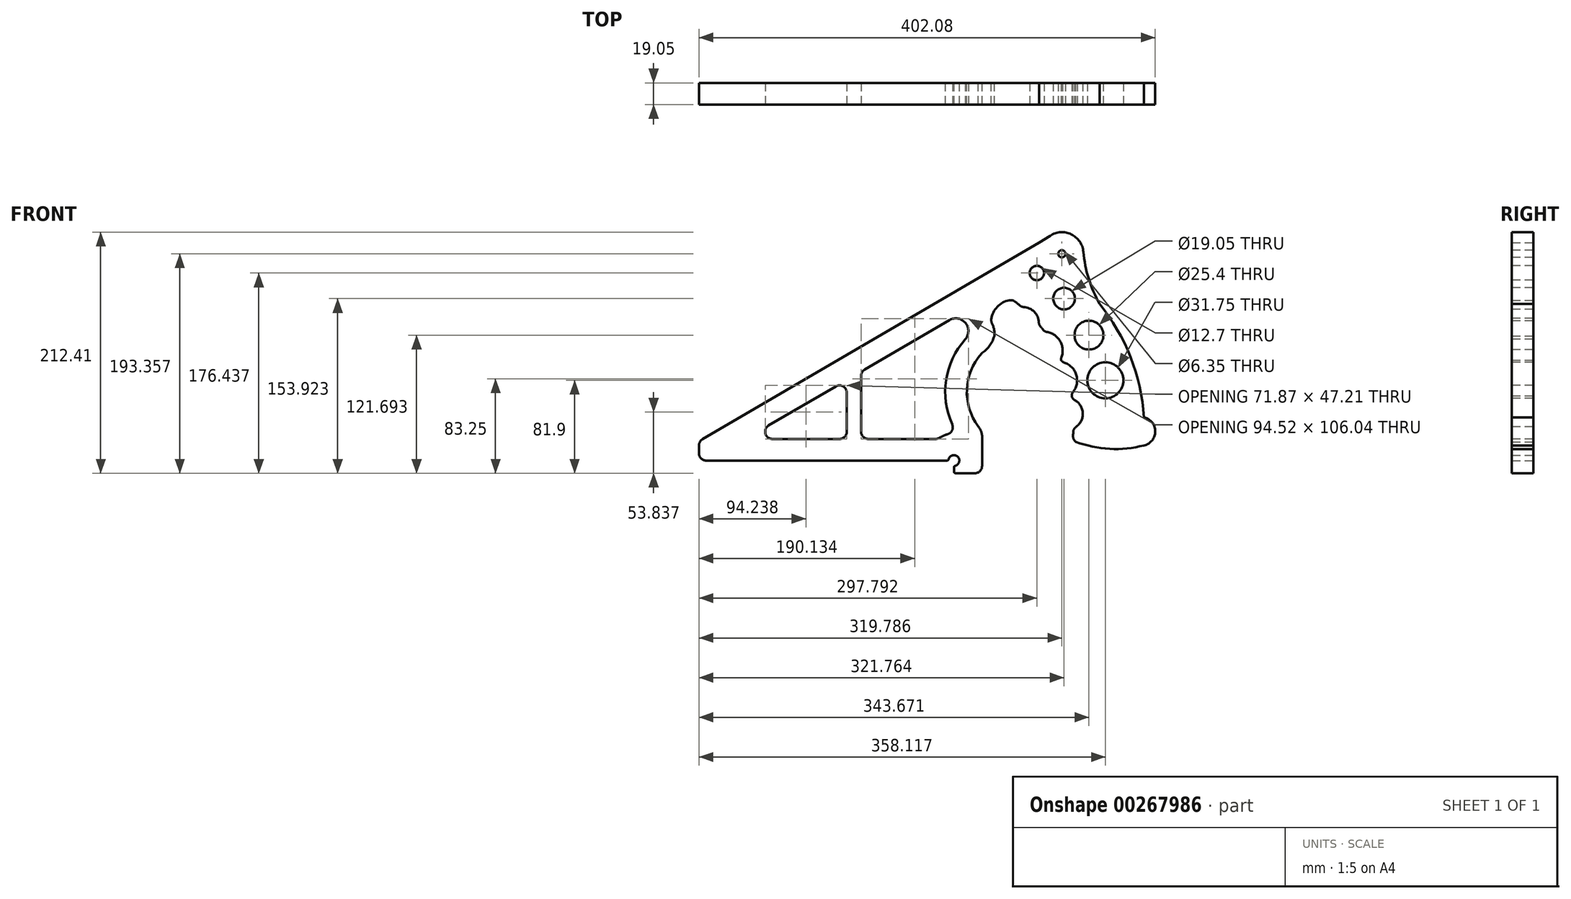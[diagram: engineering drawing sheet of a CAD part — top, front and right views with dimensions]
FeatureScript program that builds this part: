
annotation { "Feature Type Name" : "Feature", "Feature Type Description" : "" }
export const myFeature = defineFeature(function(context is Context, id is Id, definition is map)
    precondition{}
    {
        {
            var Q0;
            Q0=qCreatedBy(makeId("Front.planeOp"),FACE);
            var sketch = newSketch(context, id + "F0", { "sketchPlane" : qUnion([Q0])});
            skLineSegment(sketch, "E0.bottom", {"start": v(-91.32, -38.1) * mm, "end": v(120.85, -38.1) * mm});
            skPoint(sketch, "E0.middle", {"position": v(0, 0) * mm});
            skLineSegment(sketch, "E1.top", {"start": v(128.59, -49.28) * mm, "end": v(145.4, -49.28) * mm});
            skLineSegment(sketch, "E1.left", {"start": v(127, -44.25) * mm, "end": v(127, -47.69) * mm});
            skArc(sketch, "E2", {"start": v(128.2, -42.71) * mm, "mid": v(130.37, -34.73) * mm, "end": v(122.39, -36.9) * mm});
            skLineSegment(sketch, "E3", {"start": v(-94.52, -19.16) * mm, "end": v(202.19, 153.88) * mm});
            skPoint(sketch, "E0.left.end.orphan", {"position": v(-127, 38.1) * mm});
            skPoint(sketch, "E4.end.orphan", {"position": v(127, 38.1) * mm});
            skLineSegment(sketch, "E5", {"start": v(151.76, -42.93) * mm, "end": v(151.76, -16.62) * mm});
            skLineSegment(sketch, "E6", {"start": v(211.78, 160.08) * mm, "end": v(202.19, 153.88) * mm});
            skPoint(sketch, "E7.start.orphan", {"position": v(215.84, 59.53) * mm});
            skPoint(sketch, "E8.center.orphan", {"position": v(151.76, 56.63) * mm});
            skArc(sketch, "E9", {"start": v(152.31, 57) * mm, "mid": v(158.7, 63.4) * mm, "end": v(162.54, 71.58) * mm});
            skArc(sketch, "E10", {"start": v(175.84, 103.16) * mm, "mid": v(165.14, 97.4) * mm, "end": v(159.93, 86.43) * mm});
            skArc(sketch, "E11", {"start": v(162.54, 71.58) * mm, "mid": v(162.39, 77.31) * mm, "end": v(160.57, 82.75) * mm});
            skArc(sketch, "E12", {"start": v(231.96, -15.93) * mm, "mid": v(221.69, 49.65) * mm, "end": v(180.82, 101.95) * mm});
            skPoint(sketch, "E13.orphan", {"position": v(218.36, 0) * mm});
            skArc(sketch, "E14", {"start": v(294.53, 0) * mm, "mid": v(282.63, 53.05) * mm, "end": v(255.25, 100.03) * mm});
            skPoint(sketch, "E15.end.orphan", {"position": v(244.82, -38.46) * mm});
            skArc(sketch, "E16", {"start": v(241.09, 145.8) * mm, "mid": v(245.76, 122.17) * mm, "end": v(255.25, 100.03) * mm});
            skPoint(sketch, "E17.orphan", {"position": v(231.19, 124.47) * mm});
            skPoint(sketch, "E18.visualSharp", {"position": v(243.17, 180.37) * mm});
            skArc(sketch, "E18.filletArc", {"start": v(241.09, 145.8) * mm, "mid": v(230.46, 161.2) * mm, "end": v(211.78, 160.08) * mm});
            skPoint(sketch, "E19.visualSharp", {"position": v(151.76, -11.22) * mm});
            skArc(sketch, "E19.filletArc", {"start": v(151.76, -16.62) * mm, "mid": v(150.87, -11.96) * mm, "end": v(148.34, -7.95) * mm});
            skPoint(sketch, "E20.visualSharp", {"position": v(151.76, -49.28) * mm});
            skArc(sketch, "E20.filletArc", {"start": v(145.4, -49.28) * mm, "mid": v(149.9, -47.42) * mm, "end": v(151.76, -42.93) * mm});
            skPoint(sketch, "E21.visualSharp", {"position": v(127, -49.28) * mm});
            skArc(sketch, "E21.filletArc", {"start": v(127, -47.69) * mm, "mid": v(127.46, -48.81) * mm, "end": v(128.59, -49.28) * mm});
            skPoint(sketch, "E22.visualSharp", {"position": v(127, -42.86) * mm});
            skArc(sketch, "E22.filletArc", {"start": v(128.2, -42.71) * mm, "mid": v(127.33, -43.28) * mm, "end": v(127, -44.25) * mm});
            skPoint(sketch, "E23.visualSharp", {"position": v(122.24, -38.1) * mm});
            skArc(sketch, "E23.filletArc", {"start": v(120.85, -38.1) * mm, "mid": v(121.82, -37.77) * mm, "end": v(122.39, -36.9) * mm});
            skArc(sketch, "E24", {"start": v(151.22, 56.03) * mm, "mid": v(138.43, 24.55) * mm, "end": v(148.34, -7.95) * mm});
            skLineSegment(sketch, "E25", {"start": v(-97.67, -24.65) * mm, "end": v(-97.67, -31.75) * mm});
            skPoint(sketch, "E26.visualSharp", {"position": v(-97.67, -38.1) * mm});
            skArc(sketch, "E26.filletArc", {"start": v(-97.67, -31.75) * mm, "mid": v(-95.81, -36.24) * mm, "end": v(-91.32, -38.1) * mm});
            skPoint(sketch, "E27.visualSharp", {"position": v(-97.67, -21) * mm});
            skArc(sketch, "E27.filletArc", {"start": v(-94.52, -19.16) * mm, "mid": v(-96.83, -21.48) * mm, "end": v(-97.67, -24.65) * mm});
            skPoint(sketch, "E28.trimOffspring.end.orphan", {"position": v(151.76, 124.47) * mm});
            skPoint(sketch, "E29.visualSharp", {"position": v(231.59, -19.23) * mm});
            skArc(sketch, "E29.filletArc", {"start": v(231.96, -15.93) * mm, "mid": v(232.46, -19.1) * mm, "end": v(234.44, -21.62) * mm});
            skPoint(sketch, "E30.visualSharp", {"position": v(178.81, 103.46) * mm});
            skArc(sketch, "E30.filletArc", {"start": v(180.82, 101.95) * mm, "mid": v(178.46, 103.08) * mm, "end": v(175.84, 103.16) * mm});
            skPoint(sketch, "E31.visualSharp", {"position": v(159.77, 84.16) * mm});
            skArc(sketch, "E31.filletArc", {"start": v(159.93, 86.43) * mm, "mid": v(159.97, 84.54) * mm, "end": v(160.57, 82.75) * mm});
            skArc(sketch, "E32.filletArc", {"start": v(152.31, 57) * mm, "mid": v(151.74, 56.55) * mm, "end": v(151.22, 56.03) * mm});
            skArc(sketch, "E33", {"start": v(294.53, -24.77) * mm, "mid": v(304.4, -12.38) * mm, "end": v(294.53, 0) * mm});
            skArc(sketch, "E34", {"start": v(234.44, -21.62) * mm, "mid": v(264.25, -27.76) * mm, "end": v(294.53, -24.77) * mm});
            skSolve(sketch);
        }
        {
            var Q0;
            Q0 = qSketchRegion(id + "F0", true);
            extrude(context, id + "F1", {"entities" : qUnion([Q0]), "depth" : 19.05 * mm});
        }
        {
            var Q0;
            Q0=makeQuery(id+"F1.opExtrude","CAP_FACE",FACE,{"disambiguationData":[OSD([sQuery(id+"F0.wireOp",EDGE,"E0.bottom"),sQuery(id+"F0.wireOp",EDGE,"E1.top"),sQuery(id+"F0.wireOp",EDGE,"E1.left"),sQuery(id+"F0.wireOp",EDGE,"E2"),sQuery(id+"F0.wireOp",EDGE,"E3"),sQuery(id+"F0.wireOp",EDGE,"E5"),sQuery(id+"F0.wireOp",EDGE,"E6"),sQuery(id+"F0.wireOp",EDGE,"E9"),sQuery(id+"F0.wireOp",EDGE,"E10"),sQuery(id+"F0.wireOp",EDGE,"E11"),sQuery(id+"F0.wireOp",EDGE,"E12"),sQuery(id+"F0.wireOp",EDGE,"E14"),sQuery(id+"F0.wireOp",EDGE,"HJlxEDbY-o9fB-rilv-pvt9-RNia6tDTG9Ej"),sQuery(id+"F0.wireOp",EDGE,"E16"),sQuery(id+"F0.wireOp",EDGE,"E18.filletArc"),sQuery(id+"F0.wireOp",EDGE,"E19.filletArc"),sQuery(id+"F0.wireOp",EDGE,"E20.filletArc"),sQuery(id+"F0.wireOp",EDGE,"E21.filletArc"),sQuery(id+"F0.wireOp",EDGE,"E22.filletArc"),sQuery(id+"F0.wireOp",EDGE,"E23.filletArc"),sQuery(id+"F0.wireOp",EDGE,"E24"),sQuery(id+"F0.wireOp",EDGE,"E25"),sQuery(id+"F0.wireOp",EDGE,"E26.filletArc"),sQuery(id+"F0.wireOp",EDGE,"E27.filletArc"),sQuery(id+"F0.wireOp",EDGE,"E29.filletArc"),sQuery(id+"F0.wireOp",EDGE,"E30.filletArc"),sQuery(id+"F0.wireOp",EDGE,"E31.filletArc"),sQuery(id+"F0.wireOp",EDGE,"E32.filletArc")])],"isStart":false});
            var sketch = newSketch(context, id + "F2", { "sketchPlane" : qUnion([Q0])});
            skCircle(sketch, "E35", {"center": v(222.12, 144.08) * mm, "radius": 3.18 * mm});
            skCircle(sketch, "E36", {"center": v(200.12, 127.16) * mm, "radius": 6.35 * mm});
            skCircle(sketch, "E37", {"center": v(224.1, 104.64) * mm, "radius": 9.53 * mm});
            skCircle(sketch, "E38", {"center": v(246, 72.41) * mm, "radius": 12.7 * mm});
            skCircle(sketch, "E39", {"center": v(260.45, 32.62) * mm, "radius": 15.88 * mm});
            skLineSegment(sketch, "E40.0", {"start": v(-33.03, -19.05) * mm, "end": v(26.15, -19.05) * mm});
            skArc(sketch, "E41.0", {"start": v(137, 68.7) * mm, "mid": v(120.15, 32.93) * mm, "end": v(125.42, -6.26) * mm});
            skArc(sketch, "E42.0", {"start": v(121.18, -15.01) * mm, "mid": v(117.54, -16.25) * mm, "end": v(114.16, -18.05) * mm});
            skPoint(sketch, "E43.visualSharp", {"position": v(112.71, -19.05) * mm});
            skArc(sketch, "E43.filletArc", {"start": v(110.73, -19.05) * mm, "mid": v(112.52, -18.8) * mm, "end": v(114.16, -18.05) * mm});
            skPoint(sketch, "E44.visualSharp", {"position": v(147.3, -25.64) * mm});
            skPoint(sketch, "E45.visualSharp", {"position": v(133.01, -19.26) * mm});
            skPoint(sketch, "E46.visualSharp", {"position": v(134.23, -21.27) * mm});
            skLineSegment(sketch, "E47.0", {"start": v(-36.23, -7.21) * mm, "end": v(22.95, 27.3) * mm});
            skPoint(sketch, "E48.visualSharp", {"position": v(129.76, -14.45) * mm});
            skArc(sketch, "E48.filletArc", {"start": v(121.18, -15.01) * mm, "mid": v(125.34, -11.62) * mm, "end": v(125.42, -6.26) * mm});
            skPoint(sketch, "E49.visualSharp", {"position": v(-56.52, -19.05) * mm});
            skArc(sketch, "E49.filletArc", {"start": v(-36.23, -7.21) * mm, "mid": v(-39.16, -14.36) * mm, "end": v(-33.03, -19.05) * mm});
            skArc(sketch, "E50", {"start": v(137, 68.7) * mm, "mid": v(137.2, 83.07) * mm, "end": v(123.06, 85.68) * mm});
            skLineSegment(sketch, "E51.trimOffspring", {"start": v(193.78, 126.92) * mm, "end": v(211.78, 137.42) * mm});
            skLineSegment(sketch, "E52.0", {"start": v(45.2, -12.7) * mm, "end": v(45.2, 36.57) * mm});
            skLineSegment(sketch, "E53.0", {"start": v(32.5, -12.7) * mm, "end": v(32.5, 21.81) * mm});
            skLineSegment(sketch, "E54", {"start": v(45.2, 36.57) * mm, "end": v(45.2, 36.63) * mm});
            skLineSegment(sketch, "E55.trimOffspring", {"start": v(48.35, 42.11) * mm, "end": v(123.06, 85.68) * mm});
            skPoint(sketch, "E56.start.orphan", {"position": v(38.85, -19.05) * mm});
            skLineSegment(sketch, "E57.trimOffspring", {"start": v(51.55, -19.05) * mm, "end": v(110.73, -19.05) * mm});
            skPoint(sketch, "E58.visualSharp", {"position": v(45.2, 40.27) * mm});
            skArc(sketch, "E58.filletArc", {"start": v(48.35, 42.11) * mm, "mid": v(46.05, 39.79) * mm, "end": v(45.2, 36.63) * mm});
            skPoint(sketch, "E59.visualSharp", {"position": v(32.5, 32.87) * mm});
            skArc(sketch, "E59.filletArc", {"start": v(32.5, 21.81) * mm, "mid": v(29.32, 27.32) * mm, "end": v(22.95, 27.3) * mm});
            skPoint(sketch, "E60.visualSharp", {"position": v(45.2, -19.05) * mm});
            skArc(sketch, "E60.filletArc", {"start": v(45.2, -12.7) * mm, "mid": v(47.06, -17.2) * mm, "end": v(51.55, -19.05) * mm});
            skPoint(sketch, "E61.visualSharp", {"position": v(32.5, -19.05) * mm});
            skArc(sketch, "E61.filletArc", {"start": v(26.15, -19.05) * mm, "mid": v(30.64, -17.2) * mm, "end": v(32.5, -12.7) * mm});
            skSolve(sketch);
        }
        {
            var Q0;
            Q0 = qSketchRegion(id + "F2", true);
            extrude(context, id + "F3", {"entities" : qUnion([Q0]), "operationType" : NewBodyOperationType.REMOVE, "oppositeDirection" : true, "depth" : 25.4 * mm});
        }
        {
            var Q0;
            Q0=makeQuery(id+"F1.opExtrude","CAP_FACE",FACE,{"disambiguationData":[OSD([sQuery(id+"F0.wireOp",EDGE,"E0.bottom"),sQuery(id+"F0.wireOp",EDGE,"E1.top"),sQuery(id+"F0.wireOp",EDGE,"E1.left"),sQuery(id+"F0.wireOp",EDGE,"E2"),sQuery(id+"F0.wireOp",EDGE,"E3"),sQuery(id+"F0.wireOp",EDGE,"E5"),sQuery(id+"F0.wireOp",EDGE,"E6"),sQuery(id+"F0.wireOp",EDGE,"E9"),sQuery(id+"F0.wireOp",EDGE,"E10"),sQuery(id+"F0.wireOp",EDGE,"E11"),sQuery(id+"F0.wireOp",EDGE,"E12"),sQuery(id+"F0.wireOp",EDGE,"E14"),sQuery(id+"F0.wireOp",EDGE,"HJlxEDbY-o9fB-rilv-pvt9-RNia6tDTG9Ej"),sQuery(id+"F0.wireOp",EDGE,"E16"),sQuery(id+"F0.wireOp",EDGE,"E18.filletArc"),sQuery(id+"F0.wireOp",EDGE,"E19.filletArc"),sQuery(id+"F0.wireOp",EDGE,"E20.filletArc"),sQuery(id+"F0.wireOp",EDGE,"E21.filletArc"),sQuery(id+"F0.wireOp",EDGE,"E22.filletArc"),sQuery(id+"F0.wireOp",EDGE,"E23.filletArc"),sQuery(id+"F0.wireOp",EDGE,"E24"),sQuery(id+"F0.wireOp",EDGE,"E25"),sQuery(id+"F0.wireOp",EDGE,"E26.filletArc"),sQuery(id+"F0.wireOp",EDGE,"E27.filletArc"),sQuery(id+"F0.wireOp",EDGE,"E29.filletArc"),sQuery(id+"F0.wireOp",EDGE,"E30.filletArc"),sQuery(id+"F0.wireOp",EDGE,"E31.filletArc"),sQuery(id+"F0.wireOp",EDGE,"E32.filletArc")])],"isStart":false});
            var sketch = newSketch(context, id + "F4", { "sketchPlane" : qUnion([Q0])});
            skArc(sketch, "E62.0", {"start": v(212.95, 45.86) * mm, "mid": v(197.09, 72.54) * mm, "end": v(175.03, 94.39) * mm});
            skLineSegment(sketch, "E63", {"start": v(212.95, 45.86) * mm, "end": v(201.25, 40.2) * mm});
            skLineSegment(sketch, "E64", {"start": v(212.95, 45.86) * mm, "end": v(218.28, 48.42) * mm});
            skLineSegment(sketch, "E65", {"start": v(197.09, 72.54) * mm, "end": v(191.86, 67.8) * mm});
            skCircle(sketch, "E66", {"center": v(187.8, 83.11) * mm, "radius": 14.07 * mm});
            skCircle(sketch, "E67", {"center": v(206.35, 58.88) * mm, "radius": 16.5 * mm});
            skCircle(sketch, "E68.MirrorC", {"center": v(219.05, 32.6) * mm, "radius": 16.5 * mm});
            skCircle(sketch, "E69.MirrorC", {"center": v(226.51, 3) * mm, "radius": 14.07 * mm});
            skSolve(sketch);
        }
        {
            var Q0;
            Q0 = qSketchRegion(id + "F4", true);
            extrude(context, id + "F5", {"entities" : qUnion([Q0]), "operationType" : NewBodyOperationType.REMOVE, "oppositeDirection" : true, "depth" : 25.4 * mm});
        }
        {
            var Q0;
            {var subQ0=sQuery(id+"F4.wireOp",EDGE,"E67");var subQ1=sQuery(id+"F0.wireOp",EDGE,"E12");var subQ2=makeQuery(id+"F1.opExtrude","CAP_EDGE",EDGE,{"disambiguationData":[OSD([subQ1])],"isStart":false});var subQ3=makeQuery(id+"F4.imprint","INTERSECT",VERTEX,{"disambiguationData":[OD(0.0)],"derivedFrom":[subQ2,subQ0]});Q0=makeQuery(id+"F5.boolean.opBoolean","INTERSECT",EDGE,{"disambiguationData":[OD(1.0)],"derivedFrom":[makeQuery(id+"F1.opExtrude","SWEPT_FACE",FACE,{"disambiguationData":[OSD([subQ1])]}),makeQuery(id+"F5.opExtrude","SWEPT_FACE",FACE,{"disambiguationData":[OSD([subQ0]),TDD([makeQuery(id+"F4.imprint","IMPRINT",EDGE,{"disambiguationData":[TD([[subQ3,-1.0]])],"derivedFrom":subQ0}),makeQuery(id+"F4.imprint","IMPRINT",EDGE,{"disambiguationData":[TD([[makeQuery(id+"F4.imprint","INTERSECT",VERTEX,{"derivedFrom":[subQ0,sQuery(id+"F4.wireOp",EDGE,"E68.MirrorC")]}),-1.0]])],"derivedFrom":subQ0}),makeQuery(id+"F4.imprint","IMPRINT",EDGE,{"disambiguationData":[TD([[subQ3,1.0]])],"derivedFrom":subQ0})])]})]});}
            var Q1;
            {var subQ0=sQuery(id+"F4.wireOp",EDGE,"E68.MirrorC");var subQ1=sQuery(id+"F0.wireOp",EDGE,"E12");var subQ2=makeQuery(id+"F1.opExtrude","CAP_EDGE",EDGE,{"disambiguationData":[OSD([subQ1])],"isStart":false});var subQ3=makeQuery(id+"F4.imprint","INTERSECT",VERTEX,{"disambiguationData":[OD(0.0)],"derivedFrom":[subQ2,subQ0]});Q1=makeQuery(id+"F5.boolean.opBoolean","INTERSECT",EDGE,{"disambiguationData":[OD(0.0)],"derivedFrom":[makeQuery(id+"F1.opExtrude","SWEPT_FACE",FACE,{"disambiguationData":[OSD([subQ1])]}),makeQuery(id+"F5.opExtrude","SWEPT_FACE",FACE,{"disambiguationData":[OSD([subQ0]),TDD([makeQuery(id+"F4.imprint","IMPRINT",EDGE,{"disambiguationData":[TD([[makeQuery(id+"F4.imprint","INTERSECT",VERTEX,{"disambiguationData":[OD(1.0)],"derivedFrom":[subQ0,sQuery(id+"F4.wireOp",EDGE,"E69.MirrorC")]}),1.0]])],"derivedFrom":subQ0}),makeQuery(id+"F4.imprint","IMPRINT",EDGE,{"disambiguationData":[TD([[makeQuery(id+"F4.imprint","INTERSECT",VERTEX,{"derivedFrom":[sQuery(id+"F4.wireOp",EDGE,"E67"),subQ0]}),-1.0]])],"derivedFrom":subQ0}),makeQuery(id+"F4.imprint","IMPRINT",EDGE,{"disambiguationData":[TD([[subQ3,1.0]])],"derivedFrom":subQ0})])]})]});}
            var Q2;
            {var subQ0=sQuery(id+"F4.wireOp",EDGE,"E67");var subQ1=sQuery(id+"F0.wireOp",EDGE,"E12");var subQ2=makeQuery(id+"F1.opExtrude","CAP_EDGE",EDGE,{"disambiguationData":[OSD([subQ1])],"isStart":false});var subQ3=makeQuery(id+"F4.imprint","INTERSECT",VERTEX,{"disambiguationData":[OD(0.0)],"derivedFrom":[subQ2,subQ0]});Q2=makeQuery(id+"F5.boolean.opBoolean","INTERSECT",EDGE,{"disambiguationData":[OD(0.0)],"derivedFrom":[makeQuery(id+"F1.opExtrude","SWEPT_FACE",FACE,{"disambiguationData":[OSD([subQ1])]}),makeQuery(id+"F5.opExtrude","SWEPT_FACE",FACE,{"disambiguationData":[OSD([subQ0]),TDD([makeQuery(id+"F4.imprint","IMPRINT",EDGE,{"disambiguationData":[TD([[subQ3,-1.0]])],"derivedFrom":subQ0}),makeQuery(id+"F4.imprint","IMPRINT",EDGE,{"disambiguationData":[TD([[makeQuery(id+"F4.imprint","INTERSECT",VERTEX,{"derivedFrom":[subQ0,sQuery(id+"F4.wireOp",EDGE,"E68.MirrorC")]}),-1.0]])],"derivedFrom":subQ0}),makeQuery(id+"F4.imprint","IMPRINT",EDGE,{"disambiguationData":[TD([[subQ3,1.0]])],"derivedFrom":subQ0})])]})]});}
            var Q3;
            Q3=makeQuery(id+"F5.boolean.opBoolean","INTERSECT",EDGE,{"disambiguationData":[OD(1.0)],"derivedFrom":[makeQuery(id+"F1.opExtrude","SWEPT_FACE",FACE,{"disambiguationData":[OSD([sQuery(id+"F0.wireOp",EDGE,"E12")])]}),makeQuery(id+"F5.opExtrude","SWEPT_FACE",FACE,{"disambiguationData":[OSD([sQuery(id+"F4.wireOp",EDGE,"E66")])]})]});
            var Q4;
            {var subQ0=sQuery(id+"F4.wireOp",EDGE,"E68.MirrorC");var subQ1=sQuery(id+"F0.wireOp",EDGE,"E12");var subQ2=makeQuery(id+"F1.opExtrude","CAP_EDGE",EDGE,{"disambiguationData":[OSD([subQ1])],"isStart":false});var subQ3=makeQuery(id+"F4.imprint","INTERSECT",VERTEX,{"disambiguationData":[OD(0.0)],"derivedFrom":[subQ2,subQ0]});Q4=makeQuery(id+"F5.boolean.opBoolean","INTERSECT",EDGE,{"disambiguationData":[OD(1.0)],"derivedFrom":[makeQuery(id+"F1.opExtrude","SWEPT_FACE",FACE,{"disambiguationData":[OSD([subQ1])]}),makeQuery(id+"F5.opExtrude","SWEPT_FACE",FACE,{"disambiguationData":[OSD([subQ0]),TDD([makeQuery(id+"F4.imprint","IMPRINT",EDGE,{"disambiguationData":[TD([[makeQuery(id+"F4.imprint","INTERSECT",VERTEX,{"disambiguationData":[OD(1.0)],"derivedFrom":[subQ0,sQuery(id+"F4.wireOp",EDGE,"E69.MirrorC")]}),1.0]])],"derivedFrom":subQ0}),makeQuery(id+"F4.imprint","IMPRINT",EDGE,{"disambiguationData":[TD([[makeQuery(id+"F4.imprint","INTERSECT",VERTEX,{"derivedFrom":[sQuery(id+"F4.wireOp",EDGE,"E67"),subQ0]}),-1.0]])],"derivedFrom":subQ0}),makeQuery(id+"F4.imprint","IMPRINT",EDGE,{"disambiguationData":[TD([[subQ3,1.0]])],"derivedFrom":subQ0})])]})]});}
            var Q5;
            Q5=makeQuery(id+"F5.boolean.opBoolean","INTERSECT",EDGE,{"disambiguationData":[OD(0.0)],"derivedFrom":[makeQuery(id+"F1.opExtrude","SWEPT_FACE",FACE,{"disambiguationData":[OSD([sQuery(id+"F0.wireOp",EDGE,"E12")])]}),makeQuery(id+"F5.opExtrude","SWEPT_FACE",FACE,{"disambiguationData":[OSD([sQuery(id+"F4.wireOp",EDGE,"E69.MirrorC")])]})]});
            var Q6;
            Q6=makeQuery(id+"F5.boolean.opBoolean","INTERSECT",EDGE,{"disambiguationData":[OD(1.0)],"derivedFrom":[makeQuery(id+"F1.opExtrude","SWEPT_FACE",FACE,{"disambiguationData":[OSD([sQuery(id+"F0.wireOp",EDGE,"E12")])]}),makeQuery(id+"F5.opExtrude","SWEPT_FACE",FACE,{"disambiguationData":[OSD([sQuery(id+"F4.wireOp",EDGE,"E69.MirrorC")])]})]});
            var Q7;
            Q7=makeQuery(id+"F5.boolean.opBoolean","INTERSECT",EDGE,{"disambiguationData":[OD(0.0)],"derivedFrom":[makeQuery(id+"F1.opExtrude","SWEPT_FACE",FACE,{"disambiguationData":[OSD([sQuery(id+"F0.wireOp",EDGE,"E12")])]}),makeQuery(id+"F5.opExtrude","SWEPT_FACE",FACE,{"disambiguationData":[OSD([sQuery(id+"F4.wireOp",EDGE,"E66")])]})]});
            fillet(context, id + "F6", {"entities" : qUnion([Q0, Q1, Q2, Q3, Q4, Q5, Q6, Q7]), "radius" : 5.08 * mm, "tangentPropagation" : true, "allowEdgeOverflow" : false});
        }
    });
